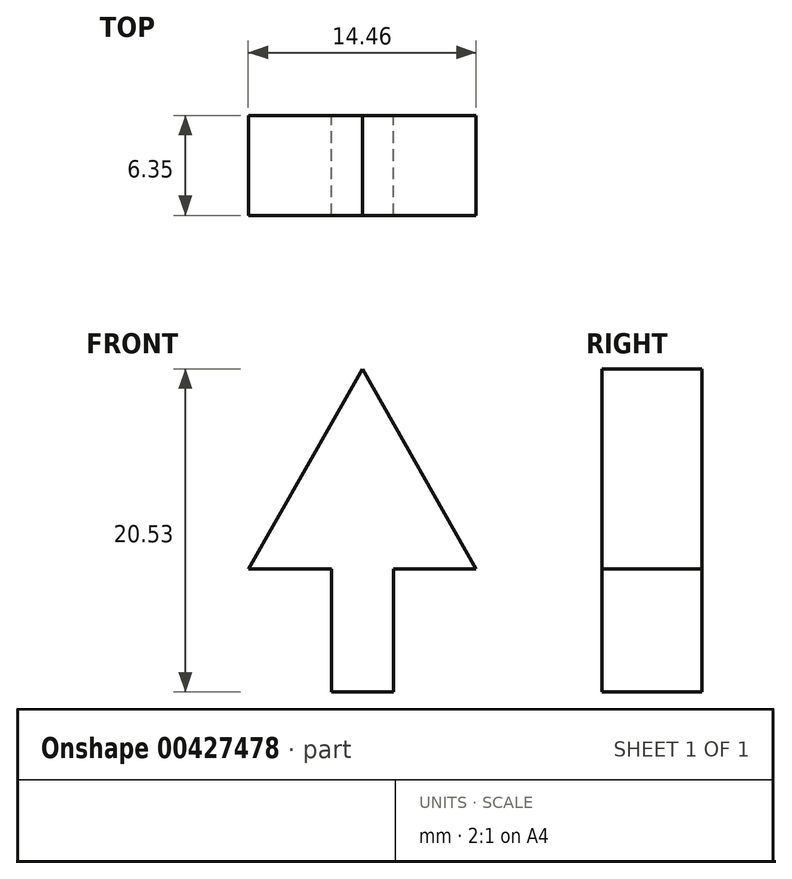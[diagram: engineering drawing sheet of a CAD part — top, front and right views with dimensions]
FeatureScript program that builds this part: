
annotation { "Feature Type Name" : "Feature", "Feature Type Description" : "" }
export const myFeature = defineFeature(function(context is Context, id is Id, definition is map)
    precondition{}
    {
        {
            var Q0;
            Q0=qCreatedBy(makeId("Front.planeOp"),FACE);
            var sketch = newSketch(context, id + "F0", { "sketchPlane" : qUnion([Q0])});
            skLineSegment(sketch, "E0.bottom", {"start": v(-5.64, -0.66) * mm, "end": v(-1.73, -0.66) * mm});
            skLineSegment(sketch, "E0.top", {"start": v(-5.64, -8.49) * mm, "end": v(-1.73, -8.49) * mm});
            skLineSegment(sketch, "E0.left", {"start": v(-5.64, -0.66) * mm, "end": v(-5.64, -8.49) * mm});
            skLineSegment(sketch, "E0.right", {"start": v(-1.73, -0.66) * mm, "end": v(-1.73, -8.49) * mm});
            skLineSegment(sketch, "E1", {"start": v(-10.94, -0.66) * mm, "end": v(3.52, -0.66) * mm});
            skLineSegment(sketch, "E2", {"start": v(-10.94, -0.66) * mm, "end": v(-3.68, 12.04) * mm});
            skLineSegment(sketch, "E3", {"start": v(3.52, -0.66) * mm, "end": v(-3.68, 12.04) * mm});
            skSolve(sketch);
        }
        {
            var Q0;
            {var subQ0=sQuery(id+"F0.wireOp",EDGE,"E2");Q0=makeQuery(id+"F0.imprint","IMPRINT",FACE,{"disambiguationData":[TD([[makeQuery(id+"F0.imprint","IMPRINT",EDGE,{"derivedFrom":subQ0}),-1.0]])]});}
            var Q1;
            Q1=makeQuery(id+"F0.imprint","IMPRINT",FACE,{"disambiguationData":[TD([[makeQuery(id+"F0.imprint","IMPRINT",EDGE,{"derivedFrom":sQuery(id+"F0.wireOp",EDGE,"E0.top")}),1.0]])]});
            extrude(context, id + "F1", {"entities" : qUnion([Q0, Q1]), "depth" : 6.35 * mm});
        }
    });
